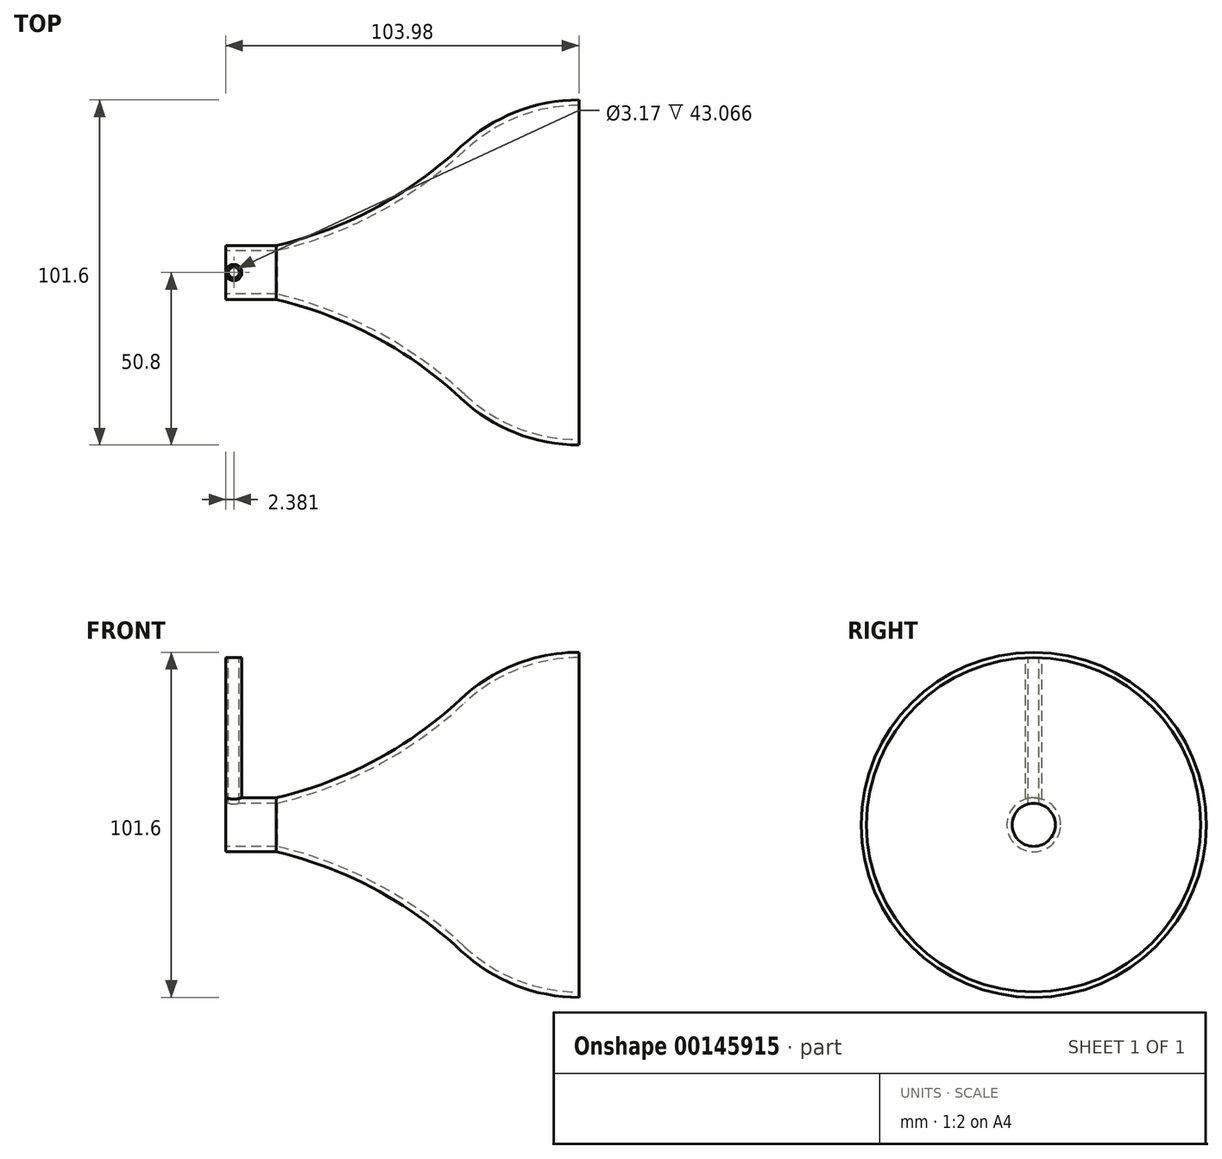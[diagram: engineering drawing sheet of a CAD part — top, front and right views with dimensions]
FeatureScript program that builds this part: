
annotation { "Feature Type Name" : "Feature", "Feature Type Description" : "" }
export const myFeature = defineFeature(function(context is Context, id is Id, definition is map)
    precondition{}
    {
        {
            assignVariable(context, id + "F0", {"name" : "WallThickness", "anyValue" : 1 / 406.4 * mm});
        }
        {
            assignVariable(context, id + "F1", {"name" : "OuterDiameter", "anyValue" : 101.6 * mm});
        }
        {
            assignVariable(context, id + "F2", {"name" : "Narrow", "anyValue" : 1 / 50.8 * mm});
        }
        {
            assignVariable(context, id + "F3", {"name" : "VacuumHeight", "anyValue" : getVariable(context, 'OuterDiameter') / 2 - getVariable(context, 'WallThickness') - getVariable(context, 'Narrow') / 2});
        }
        {
            var Q0;
            Q0=qCreatedBy(makeId("Front.planeOp"),FACE);
            var sketch = newSketch(context, id + "F4", { "sketchPlane" : qUnion([Q0])});
            skArc(sketch, "E0", {"start": v(-2.54, 51.59) * mm, "mid": v(-32.12, 62.76) * mm, "end": v(-57.82, 81.18) * mm});
            skArc(sketch, "E1", {"start": v(-57.82, 81.18) * mm, "mid": v(-73.37, 91.01) * mm, "end": v(-91.44, 94.45) * mm});
            skLineSegment(sketch, "E2", {"start": v(25.29, 170.01) * mm, "end": v(-2.54, 51.59) * mm, "construction": true});
            skLineSegment(sketch, "E3", {"start": v(25.29, 170.01) * mm, "end": v(-57.82, 81.18) * mm, "construction": true});
            skLineSegment(sketch, "E4", {"start": v(-57.82, 81.18) * mm, "end": v(-91.44, 45.24) * mm, "construction": true});
            skLineSegment(sketch, "E5", {"start": v(-91.44, 45.24) * mm, "end": v(-91.44, 51.59) * mm, "construction": true});
            skLineSegment(sketch, "E6", {"start": v(-91.44, 51.59) * mm, "end": v(-2.54, 51.59) * mm, "construction": true});
            skLineSegment(sketch, "E7", {"start": v(-91.44, 94.45) * mm, "end": v(-95.57, 94.45) * mm, "construction": true});
            skLineSegment(sketch, "E8", {"start": v(-91.44, 51.59) * mm, "end": v(-91.44, 94.45) * mm, "construction": true});
            skLineSegment(sketch, "E9", {"start": v(-91.44, 45.24) * mm, "end": v(10.16, 45.24) * mm, "construction": true});
            skLineSegment(sketch, "E10", {"start": v(10.16, 51.59) * mm, "end": v(10.16, 45.24) * mm, "construction": true});
            skArc(sketch, "E11.0", {"start": v(-56.73, 82.34) * mm, "mid": v(-72.78, 92.49) * mm, "end": v(-91.44, 96.04) * mm});
            skArc(sketch, "E11.1", {"start": v(-2.35, 53.18) * mm, "mid": v(-31.45, 64.2) * mm, "end": v(-56.73, 82.34) * mm});
            skLineSegment(sketch, "E11.2", {"start": v(-2.35, 53.18) * mm, "end": v(10.35, 53.18) * mm});
            skLineSegment(sketch, "E12", {"start": v(-91.44, 96.04) * mm, "end": v(-91.44, 94.45) * mm});
            skArc(sketch, "E13.MirrorCS", {"start": v(22.68, 53.18) * mm, "mid": v(51.77, 64.2) * mm, "end": v(77.06, 82.34) * mm});
            skLineSegment(sketch, "E14.MirrorCS", {"start": v(111.76, 51.59) * mm, "end": v(22.86, 51.59) * mm, "construction": true});
            skLineSegment(sketch, "E15.MirrorCS", {"start": v(111.76, 51.59) * mm, "end": v(111.76, 94.45) * mm, "construction": true});
            skArc(sketch, "E16.MirrorCS", {"start": v(22.86, 51.59) * mm, "mid": v(52.44, 62.76) * mm, "end": v(78.14, 81.18) * mm});
            skArc(sketch, "E17.MirrorCS", {"start": v(78.14, 81.18) * mm, "mid": v(93.69, 91.01) * mm, "end": v(111.76, 94.45) * mm});
            skLineSegment(sketch, "E18.MirrorCS", {"start": v(111.76, 96.04) * mm, "end": v(111.76, 94.45) * mm});
            skLineSegment(sketch, "E19.MirrorCS", {"start": v(22.68, 53.18) * mm, "end": v(9.98, 53.18) * mm});
            skArc(sketch, "E20.MirrorCS", {"start": v(77.06, 82.34) * mm, "mid": v(93.1, 92.49) * mm, "end": v(111.76, 96.04) * mm});
            skLineSegment(sketch, "E21.top", {"start": v(10.16, 94.45) * mm, "end": v(7.78, 94.45) * mm});
            skLineSegment(sketch, "E22", {"start": v(10.16, 51.59) * mm, "end": v(22.86, 51.59) * mm});
            skLineSegment(sketch, "E23", {"start": v(7.78, 51.59) * mm, "end": v(7.78, 94.45) * mm});
            skLineSegment(sketch, "E24", {"start": v(-2.54, 51.59) * mm, "end": v(10.16, 51.59) * mm});
            skLineSegment(sketch, "E25", {"start": v(10.16, 94.45) * mm, "end": v(10.16, 51.59) * mm});
            skSolve(sketch);
        }
        {
            var Q0;
            Q0=makeQuery(id+"F4.imprint","IMPRINT",FACE,{"disambiguationData":[TD([[makeQuery(id+"F4.imprint","IMPRINT",EDGE,{"derivedFrom":sQuery(id+"F4.wireOp",EDGE,"E0")}),-1.0]])]});
            var Q1;
            {var subQ3=sQuery(id+"F4.wireOp",EDGE,"E21.right");Q1=makeQuery(id+"F4.imprint","IMPRINT",FACE,{"disambiguationData":[TD([[makeQuery(id+"F4.imprint","IMPRINT",EDGE,{"derivedFrom":subQ3}),-1.0]])]});}
            var Q2;
            Q2=makeQuery(id+"F4.imprint","IMPRINT",FACE,{"disambiguationData":[TD([[makeQuery(id+"F4.imprint","IMPRINT",EDGE,{"derivedFrom":sQuery(id+"F4.wireOp",EDGE,"E13.MirrorCS")}),-1.0]])]});
            var Q3;
            {var subQ0=sQuery(id+"F4.wireOp",EDGE,"aa7590bf-0a54-4db5-b952-4cd879cc4bcd");Q3=makeQuery(id+"F4.imprint","IMPRINT",FACE,{"disambiguationData":[TD([[makeQuery(id+"F4.imprint","IMPRINT",EDGE,{"derivedFrom":subQ0}),1.0]])]});}
            var Q4;
            {var subQ3=sQuery(id+"F4.wireOp",EDGE,"E23");var subQ5=sQuery(id+"F4.wireOp",EDGE,"E24");var subQ7=makeQuery(id+"F4.imprint","INTERSECT",VERTEX,{"derivedFrom":[subQ3,subQ5]});Q4=makeQuery(id+"F4.imprint","IMPRINT",FACE,{"disambiguationData":[TD([[makeQuery(id+"F4.imprint","IMPRINT",EDGE,{"disambiguationData":[TD([[subQ7,-1.0]])],"derivedFrom":subQ3}),-1.0]])]});}
            var Q5;
            Q5=sQuery(id+"F4.wireOp",EDGE,"E9");
            revolve(context, id + "F5", {"entities" : qUnion([Q0, Q1, Q2, Q3, Q4]), "axis" : qUnion([Q5]), "revolveType" : RevolveType.FULL});
        }
        {
            var Q0;
            {var subQ4=sQuery(id+"F4.wireOp",EDGE,"E21.top");Q0=makeQuery(id+"F4.imprint","IMPRINT",FACE,{"disambiguationData":[TD([[makeQuery(id+"F4.imprint","IMPRINT",EDGE,{"derivedFrom":subQ4}),1.0]])]});}
            var Q1;
            {var subQ3=sQuery(id+"F4.wireOp",EDGE,"E21.right");Q1=makeQuery(id+"F4.imprint","IMPRINT",FACE,{"disambiguationData":[TD([[makeQuery(id+"F4.imprint","IMPRINT",EDGE,{"derivedFrom":subQ3}),-1.0]])]});}
            var Q2;
            {var subQ3=sQuery(id+"F4.wireOp",EDGE,"E23");var subQ5=sQuery(id+"F4.wireOp",EDGE,"E24");var subQ7=makeQuery(id+"F4.imprint","INTERSECT",VERTEX,{"derivedFrom":[subQ3,subQ5]});Q2=makeQuery(id+"F4.imprint","IMPRINT",FACE,{"disambiguationData":[TD([[makeQuery(id+"F4.imprint","IMPRINT",EDGE,{"disambiguationData":[TD([[subQ7,-1.0]])],"derivedFrom":subQ3}),-1.0]])]});}
            var Q3;
            Q3=sQuery(id+"F4.wireOp",EDGE,"E25");
            revolve(context, id + "F6", {"operationType" : NewBodyOperationType.ADD, "entities" : qUnion([Q0, Q1, Q2]), "axis" : qUnion([Q3]), "revolveType" : RevolveType.FULL});
        }
        {
            var Q0;
            Q0=makeQuery(id+"F6.opRevolve","SWEPT_FACE",FACE,{"disambiguationData":[OSD([sQuery(id+"F4.wireOp",EDGE,"E21.top")])]});
            var sketch = newSketch(context, id + "F7", { "sketchPlane" : qUnion([Q0])});
            skCircle(sketch, "E26", {"center": v(10.16, 0) * mm, "radius": 1.59 * mm});
            skSolve(sketch);
        }
        {
            var Q0;
            Q0=makeQuery(id+"F7.imprint","IMPRINT",FACE,{"disambiguationData":[TD([[makeQuery(id+"F7.imprint","IMPRINT",EDGE,{"derivedFrom":sQuery(id+"F7.wireOp",EDGE,"E26")}),1.0]])]});
            extrude(context, id + "F8", {"entities" : qUnion([Q0]), "operationType" : NewBodyOperationType.REMOVE, "oppositeDirection" : true, "depth" : getVariable(context, 'VacuumHeight') + getVariable(context, 'WallThickness')});
        }
    });
